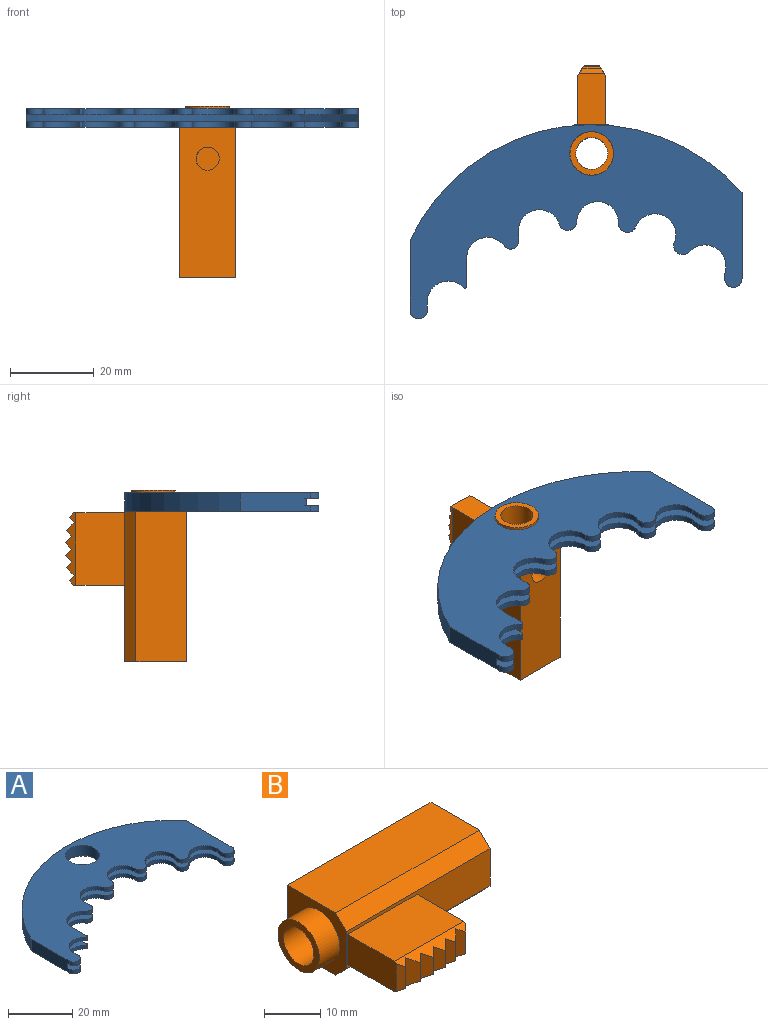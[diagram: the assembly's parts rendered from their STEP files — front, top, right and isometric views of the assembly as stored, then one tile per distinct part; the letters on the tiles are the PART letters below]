
ASSEMBLY  parts=2 mates=1
PART A: 44 faces, bbox 79.5x46.5x4.5 mm
  f0: cylinder r=5mm len=10mm, axis (0,0,-1), area 23mm2, adj f1,f18,f39,f42
  f1: cylinder r=2.2mm len=4.04mm, axis (0,0,-1), area 7.6mm2, adj f0,f2,f39,f42
  f2: cylinder r=5mm len=9.74mm, axis (0,0,-1), area 23mm2, adj f1,f3,f39,f42
  f3: cylinder r=2.2mm len=3.55mm, axis (0,0,-1), area 7.6mm2, adj f2,f4,f39,f42
  f4: cylinder r=5mm len=8.92mm, axis (0,0,-1), area 18.2mm2, adj f3,f5,f39,f42
  f5: plane 2.32x1.41mm, normal (-0.99,0.11,0), area 3.3mm2, adj f4,f6,f39,f42
  f6: cylinder r=2.1mm len=4.2mm, axis (0,0,-1), area 9.6mm2, adj f5,f7,f39,f42
  f7: plane 20.65x4.5mm, normal (1,0,0), area 84.9mm2, adj f6,f25,f26,f38,f39,f41,f42,f43
  f8: plane 16.71x4.5mm, normal (-1,0,0), area 73.8mm2, adj f9,f26,f27,f38,f39,f41,f42,f43
  f9: cylinder r=2.08mm len=4.15mm, axis (0,0,-1), area 9.2mm2, adj f8,f10,f39,f42
  f10: plane 1.98x1.41mm, normal (1,0,0), area 2.8mm2, adj f9,f11,f39,f42
  f11: cylinder r=5mm len=8.67mm, axis (0,0,-1), area 16.8mm2, adj f10,f12,f39,f42
  f12: cylinder r=0.43mm len=1.41mm, axis (0,0,-1), area 1.4mm2, adj f11,f13,f39,f42
  f13: plane 6.76x1.41mm, normal (1,0,0), area 9.5mm2, adj f12,f14,f39,f42
  f14: cylinder r=5mm len=9.03mm, axis (0,0,-1), area 17.7mm2, adj f13,f15,f39,f42
  f15: cylinder r=1.88mm len=3.39mm, axis (0,0,-1), area 6.6mm2, adj f14,f16,f39,f42
  f16: plane 2.53x1.41mm, normal (1,0,0), area 3.6mm2, adj f15,f17,f39,f42
  f17: cylinder r=5mm len=9.84mm, axis (0,0,-1), area 20.3mm2, adj f16,f18,f39,f42
  f18: cylinder r=2.2mm len=4.09mm, axis (0,0,-1), area 7.6mm2, adj f0,f17,f39,f42
  f19: cylinder r=5mm len=10mm, axis (0,0,-1), area 23mm2, adj f20,f36,f38,f43
  f20: cylinder r=2.2mm len=4.04mm, axis (0,0,-1), area 7.6mm2, adj f19,f21,f38,f43
  f21: cylinder r=5mm len=9.74mm, axis (0,0,-1), area 23mm2, adj f20,f22,f38,f43
  f22: cylinder r=2.2mm len=3.55mm, axis (0,0,-1), area 7.6mm2, adj f21,f23,f38,f43
  f23: cylinder r=5mm len=8.92mm, axis (0,0,-1), area 18.2mm2, adj f22,f24,f38,f43
  f24: plane 2.32x1.41mm, normal (-0.99,0.11,0), area 3.3mm2, adj f23,f25,f38,f43
  f25: cylinder r=2.1mm len=4.2mm, axis (0,0,-1), area 9.6mm2, adj f7,f24,f38,f43
  f26: cylinder r=48mm len=79.5mm, axis (0,0,-1), area 428.2mm2, adj f7,f8,f38,f39
  f27: cylinder r=2.08mm len=4.15mm, axis (0,0,-1), area 9.2mm2, adj f8,f28,f38,f43
  f28: plane 1.98x1.41mm, normal (1,0,0), area 2.8mm2, adj f27,f29,f38,f43
  f29: cylinder r=5mm len=8.67mm, axis (0,0,-1), area 16.8mm2, adj f28,f30,f38,f43
  f30: cylinder r=0.43mm len=1.41mm, axis (0,0,-1), area 1.4mm2, adj f29,f31,f38,f43
  f31: plane 6.76x1.41mm, normal (1,0,0), area 9.5mm2, adj f30,f32,f38,f43
  f32: cylinder r=5mm len=9.03mm, axis (0,0,-1), area 17.7mm2, adj f31,f33,f38,f43
  f33: cylinder r=1.88mm len=3.39mm, axis (0,0,-1), area 6.6mm2, adj f32,f34,f38,f43
  f34: plane 2.53x1.41mm, normal (1,0,0), area 3.6mm2, adj f33,f35,f38,f43
  f35: cylinder r=5mm len=9.84mm, axis (0,0,-1), area 20.3mm2, adj f34,f36,f38,f43
  f36: cylinder r=2.2mm len=4.09mm, axis (0,0,-1), area 7.6mm2, adj f19,f35,f38,f43
  f37: cylinder r=5.25mm len=10.5mm, axis (0,0,-1), area 128.6mm2, adj f38,f40
  f38: plane 79.5x46.5mm, normal (0,0,1), area 1634.8mm2, adj f7,f8,f19,f20,f21,f22,f23,f24
  f39: plane 79.5x46.5mm, normal (0,0,-1), area 1613.8mm2, adj f0,f1,f2,f3,f4,f5,f6,f7
  f40: cone r=5.85mm half-angle=45deg, axis (0,0,-1), area 29.6mm2, adj f37,f39
  f41: cylinder r=48mm len=79.5mm, axis (0,0,1), area 160.3mm2, adj f7,f8,f42,f43
  f42: plane 79.5x30.6mm, normal (0,0,1), area 457.3mm2, adj f0,f1,f2,f3,f4,f5,f6,f7
  f43: plane 79.5x30.6mm, normal (0,0,-1), area 457.3mm2, adj f7,f8,f19,f20,f21,f22,f23,f24
PART B: 32 faces, bbox 41.1x29.1x13.5 mm
  f0: plane 17.4x11.7mm, normal (0,0,1), area 203.6mm2, adj f2,f15,f19,f24
  f1: plane 17.4x11.7mm, normal (0,0,-1), area 203.6mm2, adj f2,f15,f19,f25
  f2: plane 12.19x6.6mm, normal (-1,0,0), area 80.3mm2, adj f0,f1,f3,f19,f24,f25
  f3: plane 6.04x1.14mm, normal (-0.71,-0.71,0), area 8.7mm2, adj f2,f4,f24,f25
  f4: plane 6.15x1.24mm, normal (0.71,-0.71,0), area 9.5mm2, adj f3,f5,f24,f25
  f5: plane 6.15x1.88mm, normal (-0.71,-0.71,0), area 13.5mm2, adj f4,f6,f24,f25
  f6: plane 5.52x1.34mm, normal (0.71,-0.71,0), area 9mm2, adj f5,f7,f24,f25
  f7: plane 5.52x1.63mm, normal (-0.71,-0.71,0), area 10.6mm2, adj f6,f8,f24,f25
  f8: plane 5.33x1.46mm, normal (0.71,-0.71,0), area 9.3mm2, adj f7,f9,f24,f25
  f9: plane 5.33x1.46mm, normal (-0.71,-0.71,0), area 9.3mm2, adj f8,f10,f24,f25
  f10: plane 5.52x1.63mm, normal (0.71,-0.71,0), area 10.6mm2, adj f9,f11,f24,f25
  f11: plane 5.52x1.34mm, normal (-0.71,-0.71,0), area 9mm2, adj f10,f12,f24,f25
  f12: plane 6.15x1.88mm, normal (0.71,-0.71,0), area 13.5mm2, adj f11,f13,f24,f25
  f13: plane 6.15x1.24mm, normal (-0.71,-0.71,0), area 9.5mm2, adj f12,f14,f24,f25
  f14: plane 6.04x1.14mm, normal (0.71,-0.71,0), area 8.7mm2, adj f13,f15,f24,f25
  f15: plane 12.19x6.6mm, normal (1,0,0), area 80.3mm2, adj f0,f1,f14,f19,f24,f25
  f16: plane 14.8x13.5mm, normal (1,0,0), area 146.6mm2, adj f17,f19,f20,f21,f22,f23,f26
  f17: plane 36x13.5mm, normal (0,1,0), area 461.7mm2, adj f16,f18,f20,f21,f31
  f18: plane 14.8x13.5mm, normal (-1,0,0), area 107.9mm2, adj f17,f19,f20,f21,f22,f23,f27
  f19: plane 36x8.1mm, normal (0,-1,0), area 176.8mm2, adj f0,f1,f2,f15,f16,f18,f22,f23
  f20: plane 36x12.1mm, normal (0,0,1), area 435.6mm2, adj f16,f17,f18,f23
  f21: plane 36x12.1mm, normal (0,0,-1), area 435.6mm2, adj f16,f17,f18,f22
  f22: plane 36x2.7mm, normal (0,-0.71,-0.71), area 137.5mm2, adj f16,f18,f19,f21
  f23: plane 36x2.7mm, normal (0,-0.71,0.71), area 137.5mm2, adj f16,f18,f19,f20
  f24: plane 17.4x2.56mm, normal (0,-0.5,0.87), area 29.2mm2, adj f0,f2,f3,f4,f5,f6,f7,f8
  f25: plane 17.4x2.56mm, normal (0,-0.5,-0.87), area 29.2mm2, adj f1,f2,f3,f4,f5,f6,f7,f8
  f26: cylinder r=3.82mm len=41.1mm, axis (1,0,0), area 934.4mm2, adj f16,f28,f30,f31
  f27: cylinder r=5.19mm len=10.38mm, axis (1,0,0), area 166.3mm2, adj f18,f28
  f28: plane 10.38x10.38mm, normal (-1,0,0), area 38.8mm2, adj f26,f27
  f29: plane 5.56x5.56mm, normal (0,1,0), area 24.3mm2, adj f30
  f30: cylinder r=2.78mm len=14.08mm, axis (0,1,0), area 234.9mm2, adj f26,f29
  f31: cylinder r=2.78mm len=5.56mm, axis (0,1,0), area 81.2mm2, adj f17,f26
PLACE A at identity fixed
PLACE B rot(axis=(-0.71,0,0.71),180deg) t=(0,63.9,-38.25)mm
MATE fastened B.f26 <-> A.f37  axis (0,0,-1) through (0,57,-2.25)mm
